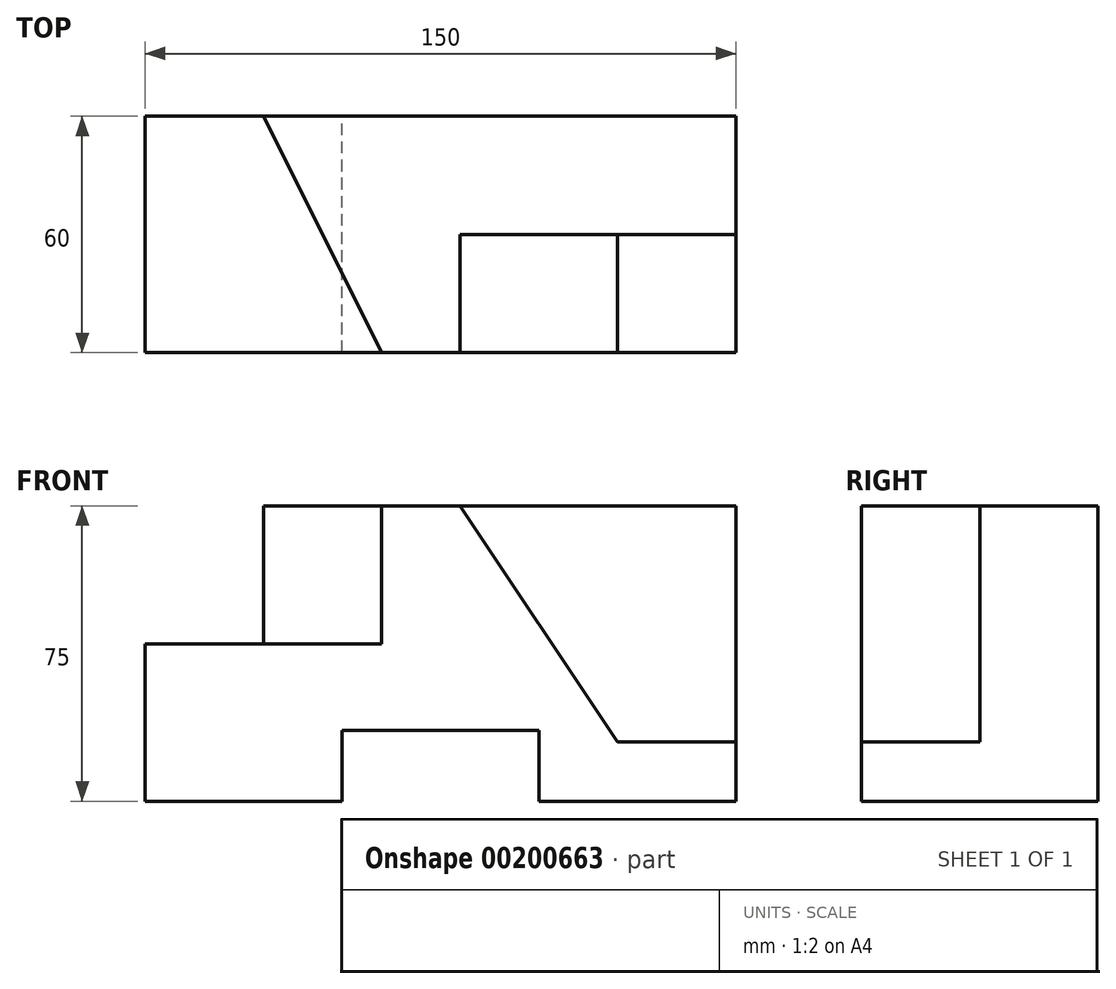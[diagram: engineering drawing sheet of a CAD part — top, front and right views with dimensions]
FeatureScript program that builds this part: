
annotation { "Feature Type Name" : "Feature", "Feature Type Description" : "" }
export const myFeature = defineFeature(function(context is Context, id is Id, definition is map)
    precondition{}
    {
        {
            var Q0;
            Q0=qCreatedBy(makeId("Front.planeOp"),FACE);
            var sketch = newSketch(context, id + "F0", { "sketchPlane" : qUnion([Q0])});
            skLineSegment(sketch, "E0", {"start": v(-75, 0) * mm, "end": v(-25, 0) * mm});
            skLineSegment(sketch, "E1", {"start": v(-25, 0) * mm, "end": v(-25, 18) * mm});
            skLineSegment(sketch, "E2", {"start": v(-25, 18) * mm, "end": v(25, 18) * mm});
            skLineSegment(sketch, "E3", {"start": v(25, 18) * mm, "end": v(25, 0) * mm});
            skLineSegment(sketch, "E4", {"start": v(25, 0) * mm, "end": v(75, 0) * mm});
            skLineSegment(sketch, "E5", {"start": v(75, 0) * mm, "end": v(75, 75) * mm});
            skLineSegment(sketch, "E6", {"start": v(75, 75) * mm, "end": v(-45, 75) * mm});
            skLineSegment(sketch, "E7", {"start": v(-45, 75) * mm, "end": v(-45, 40) * mm});
            skLineSegment(sketch, "E8", {"start": v(-45, 40) * mm, "end": v(-75, 40) * mm});
            skLineSegment(sketch, "E9", {"start": v(-75, 40) * mm, "end": v(-75, 0) * mm});
            skSolve(sketch);
        }
        {
            var Q0;
            Q0=makeQuery(id+"F0.imprint","IMPRINT",FACE,{"disambiguationData":[TD([[makeQuery(id+"F0.imprint","IMPRINT",EDGE,{"derivedFrom":sQuery(id+"F0.wireOp",EDGE,"E0")}),1.0]])]});
            extrude(context, id + "F1", {"entities" : qUnion([Q0]), "depth" : 60 * mm});
        }
        {
            var Q0;
            Q0=makeQuery(id+"F1.opExtrude","CAP_FACE",FACE,{"disambiguationData":[OSD([sQuery(id+"F0.wireOp",EDGE,"E0"),sQuery(id+"F0.wireOp",EDGE,"E1"),sQuery(id+"F0.wireOp",EDGE,"E2"),sQuery(id+"F0.wireOp",EDGE,"E3"),sQuery(id+"F0.wireOp",EDGE,"E4"),sQuery(id+"F0.wireOp",EDGE,"E5"),sQuery(id+"F0.wireOp",EDGE,"E6"),sQuery(id+"F0.wireOp",EDGE,"E7"),sQuery(id+"F0.wireOp",EDGE,"E8"),sQuery(id+"F0.wireOp",EDGE,"E9")])],"isStart":false});
            var sketch = newSketch(context, id + "F2", { "sketchPlane" : qUnion([Q0])});
            skLineSegment(sketch, "E10.0", {"start": v(75, 75) * mm, "end": v(-45, 75) * mm});
            skLineSegment(sketch, "E11", {"start": v(75, 15) * mm, "end": v(45, 15) * mm});
            skLineSegment(sketch, "E12", {"start": v(45, 15) * mm, "end": v(5, 75) * mm});
            skSolve(sketch);
        }
        {
            var Q0;
            {var subQ4=sQuery(id+"F2.wireOp",EDGE,"E11");Q0=makeQuery(id+"F2.imprint","IMPRINT",FACE,{"disambiguationData":[TD([[makeQuery(id+"F2.imprint","IMPRINT",EDGE,{"derivedFrom":subQ4}),-1.0]])]});}
            extrude(context, id + "F3", {"entities" : qUnion([Q0]), "operationType" : NewBodyOperationType.REMOVE, "oppositeDirection" : true, "depth" : 30 * mm});
        }
        {
            var Q0;
            Q0=makeQuery(id+"F1.opExtrude","SWEPT_FACE",FACE,{"disambiguationData":[OSD([sQuery(id+"F0.wireOp",EDGE,"E6")])]});
            var sketch = newSketch(context, id + "F4", { "sketchPlane" : qUnion([Q0])});
            skLineSegment(sketch, "E13.0", {"start": v(75, 0) * mm, "end": v(-45, 0) * mm});
            skLineSegment(sketch, "E14.0", {"start": v(-45, -60) * mm, "end": v(-45, 0) * mm});
            skLineSegment(sketch, "E15.0", {"start": v(5, -60) * mm, "end": v(-45, -60) * mm});
            skPoint(sketch, "E16.0", {"position": v(5, -45) * mm});
            skLineSegment(sketch, "E17.0", {"start": v(5, -30) * mm, "end": v(5, -60) * mm});
            skLineSegment(sketch, "E18.0", {"start": v(75, -30) * mm, "end": v(5, -30) * mm});
            skLineSegment(sketch, "E19.0", {"start": v(75, -30) * mm, "end": v(75, 0) * mm});
            skLineSegment(sketch, "E20.0.0", {"start": v(-45, 0) * mm, "end": v(-75, 0) * mm});
            skLineSegment(sketch, "E20.0.1", {"start": v(-75, 0) * mm, "end": v(-75, -60) * mm});
            skLineSegment(sketch, "E20.0.2", {"start": v(-75, -60) * mm, "end": v(-45, -60) * mm});
            skLineSegment(sketch, "E21", {"start": v(-45, 0) * mm, "end": v(-15, -60) * mm});
            skSolve(sketch);
        }
        {
            var Q0;
            {var subQ0=sQuery(id+"F4.wireOp",EDGE,"E14.0");Q0=makeQuery(id+"F4.imprint","IMPRINT",FACE,{"disambiguationData":[TD([[makeQuery(id+"F4.imprint","IMPRINT",EDGE,{"derivedFrom":subQ0}),-1.0]])]});}
            extrude(context, id + "F5", {"entities" : qUnion([Q0]), "operationType" : NewBodyOperationType.REMOVE, "oppositeDirection" : true, "depth" : (75 - 40) * mm});
        }
    });
